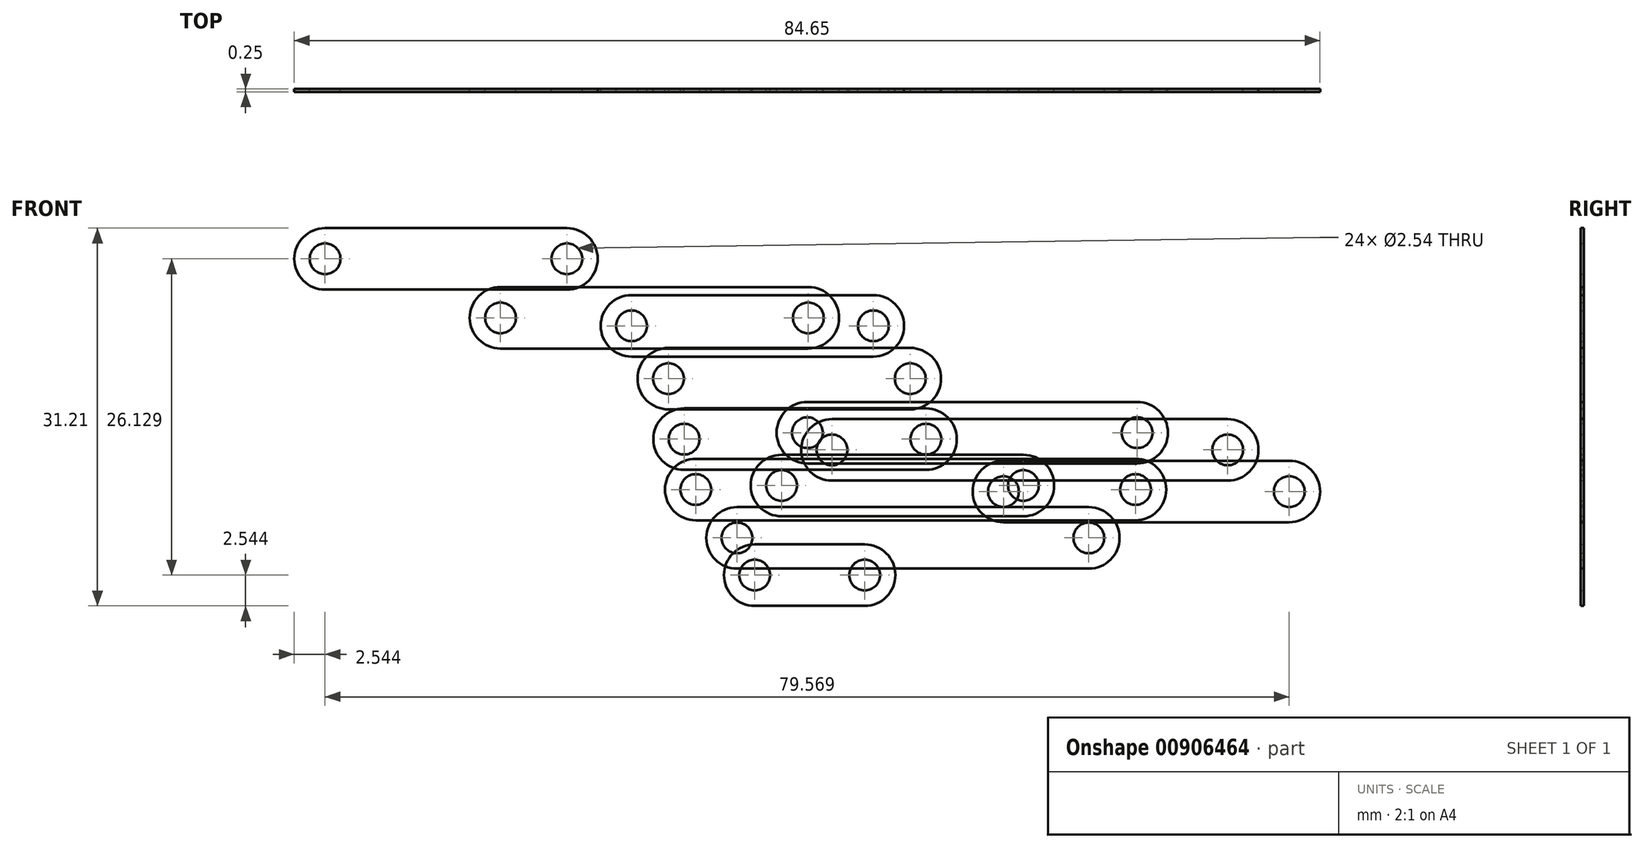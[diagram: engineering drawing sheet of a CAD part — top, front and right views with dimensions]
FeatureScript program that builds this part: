
annotation { "Feature Type Name" : "Feature", "Feature Type Description" : "" }
export const myFeature = defineFeature(function(context is Context, id is Id, definition is map)
    precondition{}
    {
        {
            assignVariable(context, id + "F0", {"name" : "thickness", "anyValue" : 0.25});
        }
        {
            var Q0;
            Q0=qCreatedBy(makeId("Front.planeOp"),FACE);
            var sketch = newSketch(context, id + "F1", { "sketchPlane" : qUnion([Q0])});
            skCircle(sketch, "E0", {"center": v(-20.38, 0) * mm, "radius": 1.27 * mm});
            skCircle(sketch, "E1", {"center": v(3.2, 0) * mm, "radius": 1.27 * mm});
            skCircle(sketch, "E2", {"center": v(-20.38, 0) * mm, "radius": 2.54 * mm});
            skCircle(sketch, "E3", {"center": v(3.2, 0) * mm, "radius": 2.54 * mm});
            skLineSegment(sketch, "E4.bottom", {"start": v(-20.38, 2.54) * mm, "end": v(3.2, 2.54) * mm});
            skLineSegment(sketch, "E4.top", {"start": v(-20.38, -2.54) * mm, "end": v(3.2, -2.54) * mm});
            skLineSegment(sketch, "E4.left", {"start": v(-20.38, 2.54) * mm, "end": v(-20.38, -2.54) * mm});
            skLineSegment(sketch, "E4.right", {"start": v(3.2, 2.54) * mm, "end": v(3.2, -2.54) * mm});
            skSolve(sketch);
        }
        {
            var Q0;
            Q0=qSketchRegion(id+"F1",true);
            extrude(context, id + "F2", {"entities" : qUnion([Q0]), "depth" : (getVariable(context, 'thickness')) * mm, "offsetDistance" : 25.4 * mm});
        }
        {
            var Q0;
            Q0=qCreatedBy(makeId("Front.planeOp"),FACE);
            var sketch = newSketch(context, id + "F3", { "sketchPlane" : qUnion([Q0])});
            skCircle(sketch, "E5", {"center": v(-40.9, -6.9) * mm, "radius": 1.27 * mm});
            skCircle(sketch, "E6", {"center": v(-31.84, -6.9) * mm, "radius": 1.27 * mm});
            skCircle(sketch, "E7", {"center": v(-40.9, -6.9) * mm, "radius": 2.54 * mm});
            skCircle(sketch, "E8", {"center": v(-31.84, -6.9) * mm, "radius": 2.54 * mm});
            skLineSegment(sketch, "E9.bottom", {"start": v(-40.9, -4.37) * mm, "end": v(-31.84, -4.37) * mm});
            skLineSegment(sketch, "E9.top", {"start": v(-40.9, -9.45) * mm, "end": v(-31.84, -9.45) * mm});
            skLineSegment(sketch, "E9.left", {"start": v(-40.9, -4.37) * mm, "end": v(-40.9, -9.45) * mm});
            skLineSegment(sketch, "E9.right", {"start": v(-31.84, -4.37) * mm, "end": v(-31.84, -9.45) * mm});
            skSolve(sketch);
        }
        {
            var Q0;
            Q0=qSketchRegion(id+"F3",true);
            extrude(context, id + "F4", {"entities" : qUnion([Q0]), "depth" : (getVariable(context, 'thickness')) * mm, "offsetDistance" : 25.4 * mm});
        }
        {
            var Q0;
            Q0=qCreatedBy(makeId("Front.planeOp"),FACE);
            var sketch = newSketch(context, id + "F5", { "sketchPlane" : qUnion([Q0])});
            skCircle(sketch, "E10", {"center": v(-42.37, -3.83) * mm, "radius": 1.27 * mm});
            skCircle(sketch, "E11", {"center": v(-13.34, -3.83) * mm, "radius": 1.27 * mm});
            skCircle(sketch, "E12", {"center": v(-42.37, -3.83) * mm, "radius": 2.54 * mm});
            skCircle(sketch, "E13", {"center": v(-13.34, -3.83) * mm, "radius": 2.54 * mm});
            skLineSegment(sketch, "E14.bottom", {"start": v(-42.37, -1.3) * mm, "end": v(-13.34, -1.3) * mm});
            skLineSegment(sketch, "E14.top", {"start": v(-42.37, -6.37) * mm, "end": v(-13.34, -6.37) * mm});
            skLineSegment(sketch, "E14.left", {"start": v(-42.37, -1.3) * mm, "end": v(-42.37, -6.37) * mm});
            skLineSegment(sketch, "E14.right", {"start": v(-13.34, -1.3) * mm, "end": v(-13.34, -6.37) * mm});
            skSolve(sketch);
        }
        {
            var Q0;
            Q0=qSketchRegion(id+"F5",true);
            extrude(context, id + "F6", {"entities" : qUnion([Q0]), "depth" : (getVariable(context, 'thickness')) * mm, "offsetDistance" : 25.4 * mm});
        }
        {
            var Q0;
            Q0=qCreatedBy(makeId("Front.planeOp"),FACE);
            var sketch = newSketch(context, id + "F7", { "sketchPlane" : qUnion([Q0])});
            skCircle(sketch, "E15", {"center": v(-48.03, 9.32) * mm, "radius": 1.27 * mm});
            skCircle(sketch, "E16", {"center": v(-28.08, 9.32) * mm, "radius": 1.27 * mm});
            skCircle(sketch, "E17", {"center": v(-48.03, 9.32) * mm, "radius": 2.54 * mm});
            skCircle(sketch, "E18", {"center": v(-28.08, 9.32) * mm, "radius": 2.54 * mm});
            skLineSegment(sketch, "E19.bottom", {"start": v(-48.03, 11.86) * mm, "end": v(-28.08, 11.86) * mm});
            skLineSegment(sketch, "E19.top", {"start": v(-48.03, 6.78) * mm, "end": v(-28.08, 6.78) * mm});
            skLineSegment(sketch, "E19.left", {"start": v(-48.03, 11.86) * mm, "end": v(-48.03, 6.78) * mm});
            skLineSegment(sketch, "E19.right", {"start": v(-28.08, 11.86) * mm, "end": v(-28.08, 6.78) * mm});
            skSolve(sketch);
        }
        {
            var Q0;
            Q0=qSketchRegion(id+"F7",true);
            extrude(context, id + "F8", {"entities" : qUnion([Q0]), "depth" : (getVariable(context, 'thickness')) * mm, "offsetDistance" : 25.4 * mm});
        }
        {
            var Q0;
            Q0=qCreatedBy(makeId("Front.planeOp"),FACE);
            var sketch = newSketch(context, id + "F9", { "sketchPlane" : qUnion([Q0])});
            skCircle(sketch, "E20", {"center": v(-38.7, 0.5) * mm, "radius": 1.27 * mm});
            skCircle(sketch, "E21", {"center": v(-18.74, 0.5) * mm, "radius": 1.27 * mm});
            skCircle(sketch, "E22", {"center": v(-38.7, 0.5) * mm, "radius": 2.54 * mm});
            skCircle(sketch, "E23", {"center": v(-18.74, 0.5) * mm, "radius": 2.54 * mm});
            skLineSegment(sketch, "E24.bottom", {"start": v(-38.7, 3.04) * mm, "end": v(-18.74, 3.04) * mm});
            skLineSegment(sketch, "E24.top", {"start": v(-38.7, -2.04) * mm, "end": v(-18.74, -2.04) * mm});
            skLineSegment(sketch, "E24.left", {"start": v(-38.7, 3.04) * mm, "end": v(-38.7, -2.04) * mm});
            skLineSegment(sketch, "E24.right", {"start": v(-18.74, 3.04) * mm, "end": v(-18.74, -2.04) * mm});
            skSolve(sketch);
        }
        {
            var Q0;
            Q0=qSketchRegion(id+"F9",true);
            extrude(context, id + "F10", {"entities" : qUnion([Q0]), "depth" : (getVariable(context, 'thickness')) * mm, "offsetDistance" : 25.4 * mm});
        }
        {
            var Q0;
            Q0=qCreatedBy(makeId("Front.planeOp"),FACE);
            var sketch = newSketch(context, id + "F11", { "sketchPlane" : qUnion([Q0])});
            skCircle(sketch, "E25", {"center": v(-36.57, 4.86) * mm, "radius": 1.27 * mm});
            skCircle(sketch, "E26", {"center": v(-9.35, 4.86) * mm, "radius": 1.27 * mm});
            skCircle(sketch, "E27", {"center": v(-36.57, 4.86) * mm, "radius": 2.54 * mm});
            skCircle(sketch, "E28", {"center": v(-9.35, 4.86) * mm, "radius": 2.54 * mm});
            skLineSegment(sketch, "E29.bottom", {"start": v(-36.57, 7.4) * mm, "end": v(-9.35, 7.4) * mm});
            skLineSegment(sketch, "E29.top", {"start": v(-36.57, 2.32) * mm, "end": v(-9.35, 2.32) * mm});
            skLineSegment(sketch, "E29.left", {"start": v(-36.57, 7.4) * mm, "end": v(-36.57, 2.32) * mm});
            skLineSegment(sketch, "E29.right", {"start": v(-9.35, 7.4) * mm, "end": v(-9.35, 2.32) * mm});
            skSolve(sketch);
        }
        {
            var Q0;
            Q0=qSketchRegion(id+"F11",true);
            extrude(context, id + "F12", {"entities" : qUnion([Q0]), "depth" : (getVariable(context, 'thickness')) * mm, "offsetDistance" : 25.4 * mm});
        }
        {
            var Q0;
            Q0=qCreatedBy(makeId("Front.planeOp"),FACE);
            var sketch = newSketch(context, id + "F13", { "sketchPlane" : qUnion([Q0])});
            skCircle(sketch, "E30", {"center": v(-34.54, 3.44) * mm, "radius": 1.27 * mm});
            skCircle(sketch, "E31", {"center": v(-1.88, 3.44) * mm, "radius": 1.27 * mm});
            skCircle(sketch, "E32", {"center": v(-34.54, 3.44) * mm, "radius": 2.54 * mm});
            skCircle(sketch, "E33", {"center": v(-1.88, 3.44) * mm, "radius": 2.54 * mm});
            skLineSegment(sketch, "E34.bottom", {"start": v(-34.54, 5.98) * mm, "end": v(-1.88, 5.98) * mm});
            skLineSegment(sketch, "E34.top", {"start": v(-34.54, 0.9) * mm, "end": v(-1.88, 0.9) * mm});
            skLineSegment(sketch, "E34.left", {"start": v(-34.54, 5.98) * mm, "end": v(-34.54, 0.9) * mm});
            skLineSegment(sketch, "E34.right", {"start": v(-1.88, 5.98) * mm, "end": v(-1.88, 0.9) * mm});
            skSolve(sketch);
        }
        {
            var Q0;
            Q0=qSketchRegion(id+"F13",true);
            extrude(context, id + "F14", {"entities" : qUnion([Q0]), "depth" : (getVariable(context, 'thickness')) * mm, "offsetDistance" : 25.4 * mm});
        }
        {
            var Q0;
            Q0=qCreatedBy(makeId("Front.planeOp"),FACE);
            var sketch = newSketch(context, id + "F15", { "sketchPlane" : qUnion([Q0])});
            skCircle(sketch, "E35", {"center": v(-51.08, 13.69) * mm, "radius": 1.27 * mm});
            skCircle(sketch, "E36", {"center": v(-31.12, 13.69) * mm, "radius": 1.27 * mm});
            skCircle(sketch, "E37", {"center": v(-51.08, 13.69) * mm, "radius": 2.54 * mm});
            skCircle(sketch, "E38", {"center": v(-31.12, 13.69) * mm, "radius": 2.54 * mm});
            skLineSegment(sketch, "E39.bottom", {"start": v(-51.08, 16.23) * mm, "end": v(-31.12, 16.23) * mm});
            skLineSegment(sketch, "E39.top", {"start": v(-51.08, 11.15) * mm, "end": v(-31.12, 11.15) * mm});
            skLineSegment(sketch, "E39.left", {"start": v(-51.08, 16.23) * mm, "end": v(-51.08, 11.15) * mm});
            skLineSegment(sketch, "E39.right", {"start": v(-31.12, 16.23) * mm, "end": v(-31.12, 11.15) * mm});
            skSolve(sketch);
        }
        {
            var Q0;
            Q0=qSketchRegion(id+"F15",true);
            extrude(context, id + "F16", {"entities" : qUnion([Q0]), "depth" : (getVariable(context, 'thickness')) * mm, "offsetDistance" : 25.4 * mm});
        }
        {
            var Q0;
            Q0=qCreatedBy(makeId("Front.planeOp"),FACE);
            var sketch = newSketch(context, id + "F17", { "sketchPlane" : qUnion([Q0])});
            skCircle(sketch, "E40", {"center": v(-76.37, 19.22) * mm, "radius": 1.27 * mm});
            skCircle(sketch, "E41", {"center": v(-56.4, 19.22) * mm, "radius": 1.27 * mm});
            skCircle(sketch, "E42", {"center": v(-76.37, 19.22) * mm, "radius": 2.54 * mm});
            skCircle(sketch, "E43", {"center": v(-56.4, 19.22) * mm, "radius": 2.54 * mm});
            skLineSegment(sketch, "E44.bottom", {"start": v(-76.37, 21.76) * mm, "end": v(-56.4, 21.76) * mm});
            skLineSegment(sketch, "E44.top", {"start": v(-76.37, 16.68) * mm, "end": v(-56.4, 16.68) * mm});
            skLineSegment(sketch, "E44.left", {"start": v(-76.37, 21.76) * mm, "end": v(-76.37, 16.68) * mm});
            skLineSegment(sketch, "E44.right", {"start": v(-56.4, 21.76) * mm, "end": v(-56.4, 16.68) * mm});
            skSolve(sketch);
        }
        {
            var Q0;
            Q0=qSketchRegion(id+"F17",true);
            extrude(context, id + "F18", {"entities" : qUnion([Q0]), "depth" : (getVariable(context, 'thickness')) * mm, "offsetDistance" : 25.4 * mm});
        }
        {
            var Q0;
            Q0=qCreatedBy(makeId("Front.planeOp"),FACE);
            var sketch = newSketch(context, id + "F19", { "sketchPlane" : qUnion([Q0])});
            skCircle(sketch, "E45", {"center": v(-46.74, 4.33) * mm, "radius": 1.27 * mm});
            skCircle(sketch, "E46", {"center": v(-26.78, 4.33) * mm, "radius": 1.27 * mm});
            skCircle(sketch, "E47", {"center": v(-46.74, 4.33) * mm, "radius": 2.54 * mm});
            skCircle(sketch, "E48", {"center": v(-26.78, 4.33) * mm, "radius": 2.54 * mm});
            skLineSegment(sketch, "E49.bottom", {"start": v(-46.74, 6.87) * mm, "end": v(-26.78, 6.87) * mm});
            skLineSegment(sketch, "E49.top", {"start": v(-46.74, 1.79) * mm, "end": v(-26.78, 1.79) * mm});
            skLineSegment(sketch, "E49.left", {"start": v(-46.74, 6.87) * mm, "end": v(-46.74, 1.79) * mm});
            skLineSegment(sketch, "E49.right", {"start": v(-26.78, 6.87) * mm, "end": v(-26.78, 1.79) * mm});
            skSolve(sketch);
        }
        {
            var Q0;
            Q0=qSketchRegion(id+"F19",true);
            extrude(context, id + "F20", {"entities" : qUnion([Q0]), "depth" : (getVariable(context, 'thickness')) * mm, "offsetDistance" : 25.4 * mm});
        }
        {
            var Q0;
            Q0=qCreatedBy(makeId("Front.planeOp"),FACE);
            var sketch = newSketch(context, id + "F21", { "sketchPlane" : qUnion([Q0])});
            skCircle(sketch, "E50", {"center": v(-45.77, 0.16) * mm, "radius": 1.27 * mm});
            skCircle(sketch, "E51", {"center": v(-9.49, 0.16) * mm, "radius": 1.27 * mm});
            skCircle(sketch, "E52", {"center": v(-45.77, 0.16) * mm, "radius": 2.54 * mm});
            skCircle(sketch, "E53", {"center": v(-9.49, 0.16) * mm, "radius": 2.54 * mm});
            skLineSegment(sketch, "E54.bottom", {"start": v(-45.77, 2.7) * mm, "end": v(-9.49, 2.7) * mm});
            skLineSegment(sketch, "E54.top", {"start": v(-45.77, -2.38) * mm, "end": v(-9.49, -2.38) * mm});
            skLineSegment(sketch, "E54.left", {"start": v(-45.77, 2.7) * mm, "end": v(-45.77, -2.38) * mm});
            skLineSegment(sketch, "E54.right", {"start": v(-9.49, 2.7) * mm, "end": v(-9.49, -2.38) * mm});
            skSolve(sketch);
        }
        {
            var Q0;
            Q0=qSketchRegion(id+"F21",true);
            extrude(context, id + "F22", {"entities" : qUnion([Q0]), "depth" : (getVariable(context, 'thickness')) * mm, "offsetDistance" : 25.4 * mm});
        }
        {
            var Q0;
            Q0=qCreatedBy(makeId("Front.planeOp"),FACE);
            var sketch = newSketch(context, id + "F23", { "sketchPlane" : qUnion([Q0])});
            skCircle(sketch, "E55", {"center": v(-61.89, 14.35) * mm, "radius": 1.27 * mm});
            skCircle(sketch, "E56", {"center": v(-36.49, 14.35) * mm, "radius": 1.27 * mm});
            skCircle(sketch, "E57", {"center": v(-61.89, 14.35) * mm, "radius": 2.54 * mm});
            skCircle(sketch, "E58", {"center": v(-36.49, 14.35) * mm, "radius": 2.54 * mm});
            skLineSegment(sketch, "E59.bottom", {"start": v(-61.89, 16.9) * mm, "end": v(-36.49, 16.9) * mm});
            skLineSegment(sketch, "E59.top", {"start": v(-61.89, 11.81) * mm, "end": v(-36.49, 11.81) * mm});
            skLineSegment(sketch, "E59.left", {"start": v(-61.89, 16.9) * mm, "end": v(-61.89, 11.81) * mm});
            skLineSegment(sketch, "E59.right", {"start": v(-36.49, 16.9) * mm, "end": v(-36.49, 11.81) * mm});
            skSolve(sketch);
        }
        {
            var Q0;
            Q0=qSketchRegion(id+"F23",true);
            extrude(context, id + "F24", {"entities" : qUnion([Q0]), "depth" : (getVariable(context, 'thickness')) * mm, "offsetDistance" : 25.4 * mm});
        }
    });
